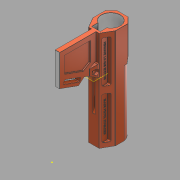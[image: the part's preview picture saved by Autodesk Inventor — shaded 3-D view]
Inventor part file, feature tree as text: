
AUTODESK INVENTOR PART (.ipt)
format: ipt  version: 2018 (Build 220112000, 112)  size: 2,685,440 bytes
history: native  units: mm
features: sketch x25, extrude x24, fillet x16, chamfer x9, plane x7, thicken_offset x6, mirror x4
ambient origin geometry x8: Origin, YZ Plane, XZ Plane, XY Plane, X Axis, Y Axis, Z Axis, Center Point
bodies: Solid1 (feature_tree)
feature tree (91):
  extrude  "Extrusion1"  Depth=159.0mm TaperAngle=0.0deg
  extrude  "Extrusion2"  Depth=20.0mm
  extrude  "Extrusion3"  Depth=12.0mm
  extrude  "Extrusion4"  Depth=102.0mm TaperAngle=0.0deg
  plane  "Work Plane1"
  mirror  "Mirror1"
  extrude  "Extrusion5"  Depth=1.0mm
  mirror  "Mirror2"
  extrude  "Extrusion6"  Depth=9.0mm
  extrude  "Extrusion7"  Depth=2.0mm
  mirror  "Mirror3"
  mirror  "Mirror4"
  plane  "Work Plane2"
  extrude  "Extrusion8"  Depth=8.0mm TaperAngle=0.0deg
  plane  "Work Plane4"
  extrude  "Extrusion9"  Depth=3.0mm
  extrude  "Extrusion10"  Depth=5.65mm TaperAngle=0.0deg
  extrude  "Extrusion11"  TaperAngle=150.0deg  [1 undecoded]
  chamfer  "Chamfer1"  Distance=27.4mm
  sketch  "Sketch15"  dims[d56=7.9mm d60=40.5mm]
  extrude  "Extrusion12"  Depth=40.5mm
  thicken_offset  "Thicken1"
  chamfer  "Chamfer2"  Distance=2.0mm
  extrude  "Extrusion13"  Depth=114.0mm TaperAngle=0.0deg
  extrude  "Extrusion14"  Depth=1.9mm
  chamfer  "Chamfer4"  Distance=2.28mm
  chamfer  "Chamfer5"  Distance=9.28mm
  fillet  "Fillet1"  Radius=12.0mm
  fillet  "Fillet2"  Radius=13.0mm
  fillet  "Fillet3"  Radius=1.0mm
  fillet  "Fillet4"  Radius=1.0mm
  fillet  "Fillet5"  Radius=14.5mm
  fillet  "Fillet6"  Radius=21.0mm
  fillet  "Fillet8"  Radius=0.25mm
  thicken_offset  "Thicken3"
  chamfer  "Chamfer6"  Distance=0.5mm
  chamfer  "Chamfer7"  Distance=0.25mm
  chamfer  "Chamfer8"  Distance=0.25mm
  extrude  "Extrusion15"  Depth=0.25mm
  extrude  "Extrusion17"  Depth=0.25mm
  sketch  "Sketch21"  dims[d79=30.0mm d80=0.0mm d82=1.9mm]
  extrude  "Extrusion18"  Depth=10.0mm
  extrude  "Extrusion19"  Depth=10.0mm
  plane  "Work Plane5"
  extrude  "Extrusion20"  Depth=10.0mm TaperAngle=60.0deg
  plane  "Work Plane6"
  extrude  "Extrusion21"  Depth=10.0mm TaperAngle=60.0deg
  plane  "Work Plane7"
  extrude  "Extrusion22"  Depth=10.0mm TaperAngle=60.0deg
  plane  "Work Plane8"
  extrude  "Extrusion16"  Depth=0.5mm TaperAngle=0.0deg
  extrude  "Extrusion23"  Depth=0.5mm TaperAngle=0.0deg
  thicken_offset  "Thicken4"
  thicken_offset  "Thicken5"
  fillet  "Fillet12"  Radius=0.5mm
  chamfer  "Chamfer10"  Distance=10.0mm
  chamfer  "Chamfer11"  Distance=4.0mm
  thicken_offset  "Thicken6"
  fillet  "Fillet14"  Radius=2.25mm
  fillet  "Fillet15"  Radius=4.0mm
  fillet  "Fillet16"  Radius=3.75mm
  sketch  "Sketch31"  dims[d116=0.25mm d117=0.5mm d118=0.25mm d119=0.25mm d120=0.25mm d122=0.25mm d125=10.0mm d126=10.0mm d127=10.0mm d128=0.75mm d129=60.0deg d130=10.0mm d131=3.25mm d132=60.0deg d133=10.0mm d134=3.25mm d135=60.0deg d136=0.5mm d137=0.0mm d138=0.5mm d139=0.0mm d140=0.5mm d141=0.0mm d142=10.0mm d143=4.0mm d144=0.0mm d145=2.25mm d146=0.0mm d148=4.0mm d149=0.0mm d150=3.75mm d151=0.0mm d152=0.5mm d153=0.0mm d154=0.5mm d155=0.0mm d163=1.0mm d164=0.0mm d167=0.25mm d168=0.4mm d169=0.4mm d170=0.4mm d171=0.4mm d172=0.4mm d173=0.7mm d174=45.0deg d175=0.4mm d176=0.7mm d177=45.0deg d178=0.4mm d179=0.4mm d181=0.5mm d182=0.25mm d183=0.25mm d184=0.4mm d185=0.4mm d186=10.0mm d187=0.0mm d188=0.25mm d189=0.25mm d190=0.25mm d191=0.25mm d204=0.25mm]
  thicken_offset  "Thicken7"
  extrude  "Extrusion24"  Depth=0.5mm TaperAngle=0.0deg
  fillet  "Fillet17"  Radius=0.5mm
  fillet  "Fillet18"  Radius=1.0mm
  fillet  "Fillet19"  Radius=0.25mm
  fillet  "Fillet20"  Radius=0.4mm
  fillet  "Fillet25"  Radius=0.4mm
  sketch  "Sketch1"  dims[d8=90.0deg d19=159.0mm d20=0.0mm]
  sketch  "Sketch2"  dims[d21=99.0mm d22=20.0mm]
  sketch  "Sketch3"  dims[d23=19.198622mm d24=12.0mm]
  sketch  "Sketch4"  dims[d25=120.0deg d27=102.0mm d28=0.0mm]
  sketch  "Sketch5"  dims[d30=6.25mm d32=1.0mm]
  sketch  "Sketch6"  dims[d33=102.0mm d34=0.0mm d36=9.0mm]
  sketch  "Sketch7"  dims[d40=11.0mm d41=2.0mm]
  sketch  "Sketch8"  dims[d42=2.0mm d43=8.0mm d44=0.0mm]
  sketch  "Sketch12"  dims[d46=19.0mm d47=3.0mm]
  sketch  "Sketch13"  dims[d49=60.0deg d50=5.65mm d51=0.0mm]
  sketch  "Sketch14"  dims[d52=3.5mm d53=150.0deg d54=27.4mm d55=0.0mm]
  sketch  "Sketch16"  dims[d61=30.0mm]
  sketch  "Sketch17"  dims[d62=13.0mm]
  sketch  "Sketch18"  dims[d63=120.0deg]
  sketch  "Sketch19"  dims[d64=19.198622mm d65=2.0mm d66=0.0mm]
  sketch  "Sketch20"  dims[d67=36.0mm d68=114.0mm d69=0.0mm]
  sketch  "Sketch22"  dims[d83=3.8mm d84=2.28mm d85=0.0mm]
  sketch  "Sketch23"  dims[d86=15.5mm d87=9.28mm d88=0.0mm]
  sketch  "Sketch25"  dims[d89=7.0mm d90=3.69mm d91=60.0deg d93=12.0mm d94=13.0mm d95=0.0mm d96=1.0mm d97=1.0mm]
  sketch  "Sketch26"  dims[d98=1.0mm d99=12.9mm d100=60.0deg d101=14.5mm d102=0.0mm d104=21.0mm d105=0.0mm]
  sketch  "Sketch27"  dims[d109=0.25mm d110=12.9mm d111=60.0deg]
  sketch  "Sketch30"  dims[d112=0.25mm d113=12.9mm d114=60.0deg d115=0.25mm]
note: 1 required parameter value undecoded (feature->parameter linkage not recoverable at this tier; creation-order binding heuristic only, values carry confidence <= 0.55)
